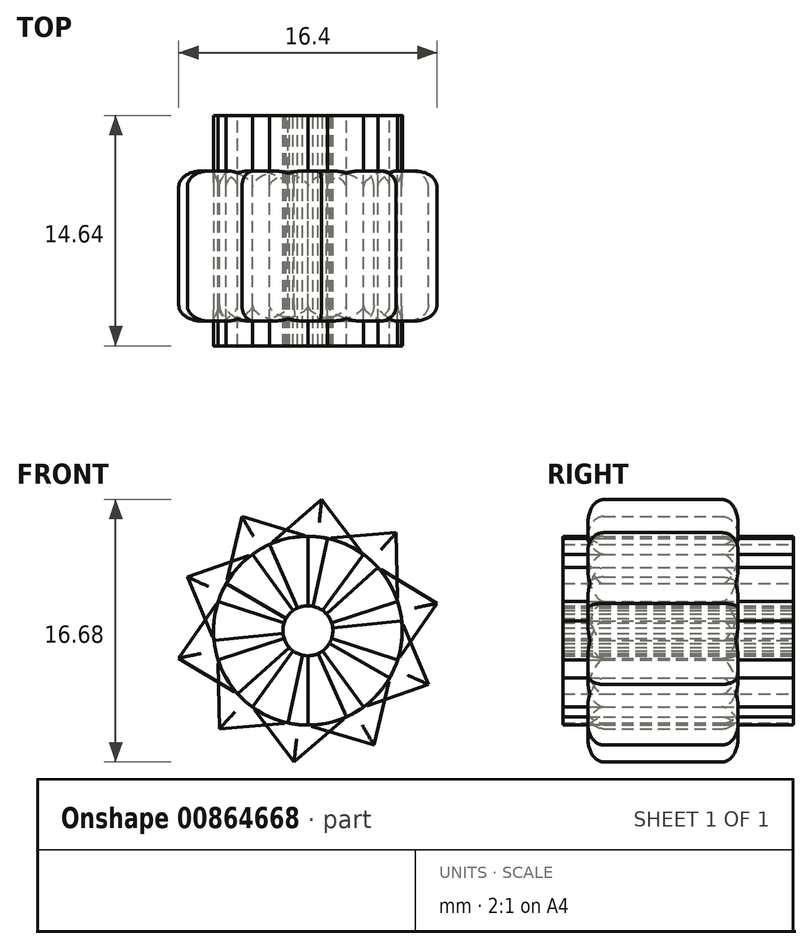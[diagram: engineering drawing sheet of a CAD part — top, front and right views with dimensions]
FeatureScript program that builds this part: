
annotation { "Feature Type Name" : "Feature", "Feature Type Description" : "" }
export const myFeature = defineFeature(function(context is Context, id is Id, definition is map)
    precondition{}
    {
        {
            var Q0;
            Q0=qCreatedBy(makeId("Front.planeOp"),FACE);
            var sketch = newSketch(context, id + "F0", { "sketchPlane" : qUnion([Q0])});
            skCircle(sketch, "E0", {"center": v(0, 0) * mm, "radius": 1.59 * mm});
            skCircle(sketch, "E1", {"center": v(0, 0) * mm, "radius": 8.38 * mm});
            skLineSegment(sketch, "E2", {"start": v(0, 0) * mm, "end": v(0, 8.38) * mm});
            skLineSegment(sketch, "E3", {"start": v(0, 0) * mm, "end": v(-7.26, 4.2) * mm});
            skLineSegment(sketch, "E4", {"start": v(0, 0) * mm, "end": v(-4.2, 7.26) * mm});
            skLineSegment(sketch, "E5", {"start": v(-4.2, 7.26) * mm, "end": v(-5.2, 3) * mm});
            skLineSegment(sketch, "E6", {"start": v(-4.2, 7.26) * mm, "end": v(0, 6) * mm});
            skCircle(sketch, "E7", {"center": v(0, 0) * mm, "radius": 6 * mm});
            skSolve(sketch);
        }
        {
            var Q0;
            {var subQ5=sQuery(id+"F0.wireOp",EDGE,"E5");Q0=makeQuery(id+"F0.imprint","IMPRINT",FACE,{"disambiguationData":[TD([[makeQuery(id+"F0.imprint","IMPRINT",EDGE,{"derivedFrom":subQ5}),1.0]])]});}
            var Q1;
            {var subQ5=sQuery(id+"F0.wireOp",EDGE,"E6");Q1=makeQuery(id+"F0.imprint","IMPRINT",FACE,{"disambiguationData":[TD([[makeQuery(id+"F0.imprint","IMPRINT",EDGE,{"derivedFrom":subQ5}),-1.0]])]});}
            extrude(context, id + "F1", {"entities" : qUnion([Q0, Q1]), "endBound" : BoundingType.SYMMETRIC, "depth" : 9.52 * mm, "offsetDistance" : 25.4 * mm});
        }
        {
            var Q0;
            {var subQ0=sQuery(id+"F0.wireOp",EDGE,"E4");var subQ1=sQuery(id+"F0.wireOp",EDGE,"E0");var subQ2=makeQuery(id+"F0.imprint","INTERSECT",VERTEX,{"derivedFrom":[subQ1,subQ0]});Q0=makeQuery(id+"F0.imprint","IMPRINT",FACE,{"disambiguationData":[TD([[makeQuery(id+"F0.imprint","IMPRINT",EDGE,{"disambiguationData":[TD([[subQ2,1.0]])],"derivedFrom":subQ1}),-1.0]])]});}
            var Q1;
            {var subQ0=sQuery(id+"F0.wireOp",EDGE,"E4");var subQ1=sQuery(id+"F0.wireOp",EDGE,"E0");var subQ2=makeQuery(id+"F0.imprint","INTERSECT",VERTEX,{"derivedFrom":[subQ1,subQ0]});Q1=makeQuery(id+"F0.imprint","IMPRINT",FACE,{"disambiguationData":[TD([[makeQuery(id+"F0.imprint","IMPRINT",EDGE,{"disambiguationData":[TD([[subQ2,-1.0]])],"derivedFrom":subQ1}),-1.0]])]});}
            extrude(context, id + "F2", {"entities" : qUnion([Q0, Q1]), "operationType" : NewBodyOperationType.ADD, "depth" : 6.35 * mm, "offsetDistance" : 25.4 * mm, "hasSecondDirection" : true, "secondDirectionOppositeDirection" : true, "secondDirectionDepth" : 8.3 * mm});
        }
        {
            var Q0;
            Q0=makeQuery(id+"F1.opExtrude","CAP_EDGE",EDGE,{"disambiguationData":[OSD([sQuery(id+"F0.wireOp",EDGE,"E5")])],"isStart":false});
            var Q1;
            Q1=makeQuery(id+"F1.opExtrude","CAP_EDGE",EDGE,{"disambiguationData":[OSD([sQuery(id+"F0.wireOp",EDGE,"E6")])],"isStart":false});
            var Q2;
            Q2=makeQuery(id+"F1.opExtrude","CAP_EDGE",EDGE,{"disambiguationData":[OSD([sQuery(id+"F0.wireOp",EDGE,"E5")])],"isStart":true});
            var Q3;
            Q3=makeQuery(id+"F1.opExtrude","CAP_EDGE",EDGE,{"disambiguationData":[OSD([sQuery(id+"F0.wireOp",EDGE,"E6")])],"isStart":true});
            fillet(context, id + "F3", {"entities" : qUnion([Q0, Q1, Q2, Q3]), "radius" : 1 * mm, "tangentPropagation" : true, "allowEdgeOverflow" : false});
        }
        {
            var Q0;
            Q0=makeQuery(id+"F1.opExtrude","SWEPT_BODY",BODY,{"disambiguationData":[OSD([sQuery(id+"F0.wireOp",EDGE,"E0"),sQuery(id+"F0.wireOp",EDGE,"E2"),sQuery(id+"F0.wireOp",EDGE,"E3"),sQuery(id+"F0.wireOp",EDGE,"E5"),sQuery(id+"F0.wireOp",EDGE,"E6")])]});
            var Q1;
            Q1=sQuery(id+"F0.wireOp",EDGE,"E0");
            circularPattern(context, id + "F4", {"entities" : qUnion([Q0]), "axis" : qUnion([Q1]), "angle" : 360 * degree, "instanceCount" : 10, "equalSpace" : true});
        }
    });
